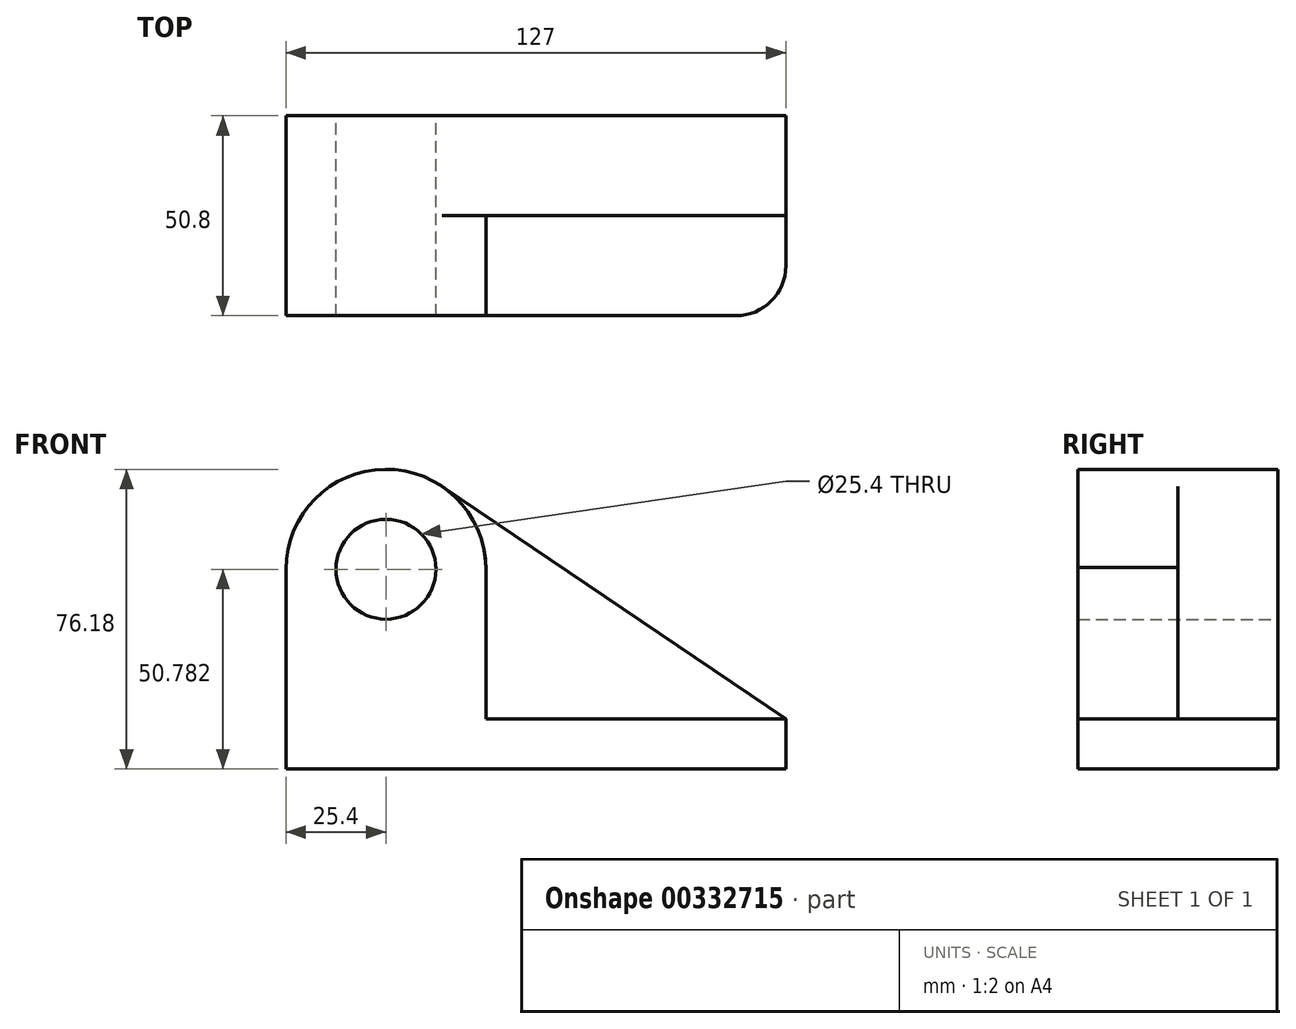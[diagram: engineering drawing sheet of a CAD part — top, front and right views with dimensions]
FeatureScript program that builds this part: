
annotation { "Feature Type Name" : "Feature", "Feature Type Description" : "" }
export const myFeature = defineFeature(function(context is Context, id is Id, definition is map)
    precondition{}
    {
        {
            var Q0;
            Q0=qCreatedBy(makeId("Front.planeOp"),FACE);
            var sketch = newSketch(context, id + "F0", { "sketchPlane" : qUnion([Q0])});
            skCircle(sketch, "E0", {"center": v(-51.04, 12.17) * mm, "radius": 12.7 * mm});
            skArc(sketch, "E1", {"start": v(-36.8, 33.2) * mm, "mid": v(-62.95, 34.6) * mm, "end": v(-76.44, 12.17) * mm});
            skLineSegment(sketch, "E2", {"start": v(-76.44, 12.2) * mm, "end": v(-76.44, -38.6) * mm});
            skLineSegment(sketch, "E3", {"start": v(-76.44, -38.6) * mm, "end": v(50.56, -38.6) * mm});
            skLineSegment(sketch, "E4", {"start": v(50.56, -38.6) * mm, "end": v(50.56, -25.9) * mm});
            skLineSegment(sketch, "E5", {"start": v(50.56, -25.9) * mm, "end": v(-36.8, 33.2) * mm});
            skSolve(sketch);
        }
        {
            var Q0;
            Q0 = qSketchRegion(id + "F0", true);
            extrude(context, id + "F1", {"entities" : qUnion([Q0]), "depth" : 25.4 * mm});
        }
        {
            var Q0;
            Q0=makeQuery(id+"F1.opExtrude","CAP_FACE",FACE,{"disambiguationData":[OSD([sQuery(id+"F0.wireOp",EDGE,"E0"),sQuery(id+"F0.wireOp",EDGE,"E1"),sQuery(id+"F0.wireOp",EDGE,"E2"),sQuery(id+"F0.wireOp",EDGE,"E3"),sQuery(id+"F0.wireOp",EDGE,"E4"),sQuery(id+"F0.wireOp",EDGE,"E5")])],"isStart":false});
            var sketch = newSketch(context, id + "F2", { "sketchPlane" : qUnion([Q0])});
            skCircle(sketch, "E6", {"center": v(-51.04, 12.17) * mm, "radius": 12.7 * mm});
            skArc(sketch, "E7", {"start": v(-25.64, 11.74) * mm, "mid": v(-50.82, 37.57) * mm, "end": v(-76.44, 12.17) * mm});
            skLineSegment(sketch, "E8.bottom", {"start": v(-76.44, -38.6) * mm, "end": v(50.56, -38.6) * mm});
            skLineSegment(sketch, "E8.top", {"start": v(-25.64, -25.9) * mm, "end": v(50.56, -25.9) * mm});
            skLineSegment(sketch, "E8.left", {"start": v(-76.44, -38.6) * mm, "end": v(-76.44, -25.9) * mm});
            skLineSegment(sketch, "E8.right", {"start": v(50.56, -38.6) * mm, "end": v(50.56, -25.9) * mm});
            skLineSegment(sketch, "E9", {"start": v(-25.64, 12.6) * mm, "end": v(-25.64, -25.9) * mm});
            skLineSegment(sketch, "E10", {"start": v(-76.44, 12.2) * mm, "end": v(-76.44, -25.9) * mm});
            skSolve(sketch);
        }
        {
            var Q0;
            Q0=makeQuery(id+"F2.imprint","IMPRINT",FACE,{"disambiguationData":[TD([[makeQuery(id+"F2.imprint","IMPRINT",EDGE,{"derivedFrom":sQuery(id+"F2.wireOp",EDGE,"E6")}),-1.0]])]});
            extrude(context, id + "F3", {"entities" : qUnion([Q0]), "operationType" : NewBodyOperationType.ADD, "depth" : 25.4 * mm});
        }
        {
            var Q0;
            Q0=makeQuery(id+"F3.opExtrude","CAP_EDGE",EDGE,{"disambiguationData":[OSD([sQuery(id+"F2.wireOp",EDGE,"E8.right")])],"isStart":false});
            fillet(context, id + "F4", {"entities" : qUnion([Q0]), "radius" : 12.7 * mm, "tangentPropagation" : true, "allowEdgeOverflow" : false});
        }
    });
